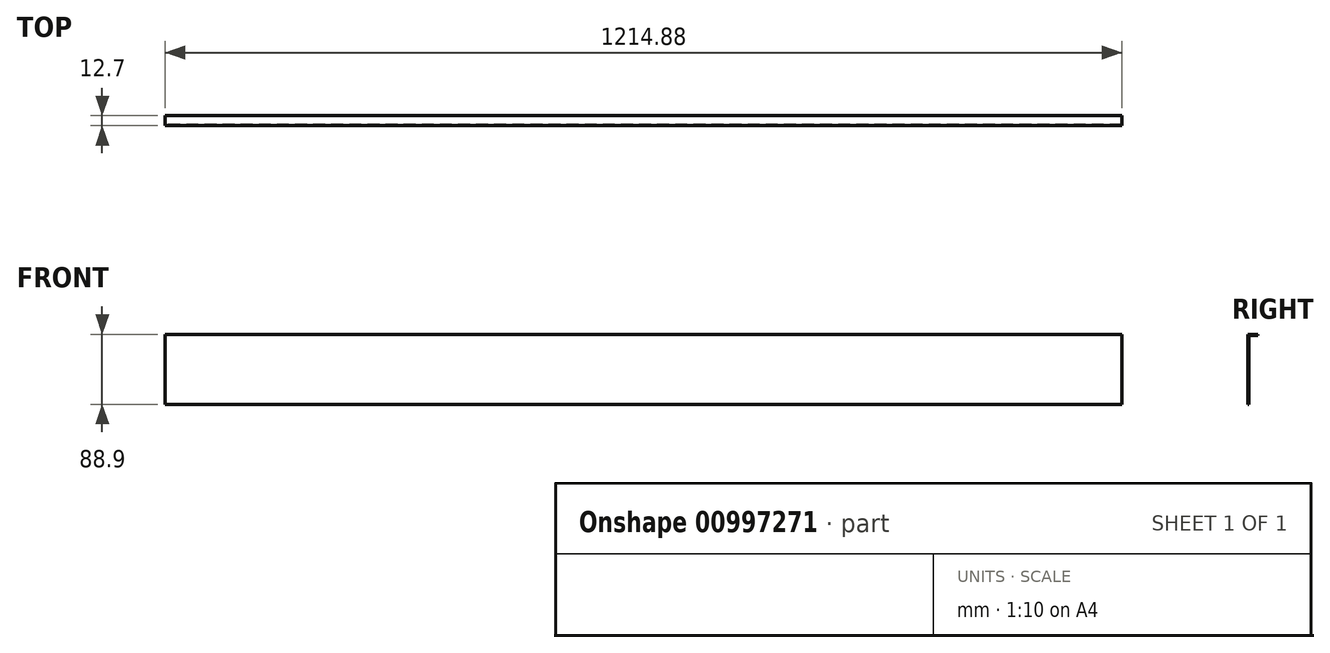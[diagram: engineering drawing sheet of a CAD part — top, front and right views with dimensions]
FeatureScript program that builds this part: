
annotation { "Feature Type Name" : "Feature", "Feature Type Description" : "" }
export const myFeature = defineFeature(function(context is Context, id is Id, definition is map)
    precondition{}
    {
        {
            var Q0;
            Q0=qCreatedBy(makeId("Right.planeOp"),FACE);
            var sketch = newSketch(context, id + "F0", { "sketchPlane" : qUnion([Q0])});
            skLineSegment(sketch, "E0.top", {"start": v(-0.63, -50.8) * mm, "end": v(0.64, -50.8) * mm});
            skLineSegment(sketch, "E0.left", {"start": v(-0.64, 38.1) * mm, "end": v(-0.63, -50.8) * mm});
            skLineSegment(sketch, "E0.right", {"start": v(0.63, 36.83) * mm, "end": v(0.64, -50.8) * mm});
            skLineSegment(sketch, "E1.top", {"start": v(0.63, 36.83) * mm, "end": v(12.06, 36.83) * mm});
            skLineSegment(sketch, "E1.right", {"start": v(12.06, 38.1) * mm, "end": v(12.06, 36.83) * mm});
            skLineSegment(sketch, "E2", {"start": v(-0.64, 38.1) * mm, "end": v(12.06, 38.1) * mm});
            skSolve(sketch);
        }
        {
            var Q0;
            Q0 = qSketchRegion(id + "F0", true);
            extrude(context, id + "F1", {"entities" : qUnion([Q0]), "endBound" : BoundingType.SYMMETRIC, "depth" : 1214.88 * mm, "offsetDistance" : 25.4 * mm});
        }
    });
